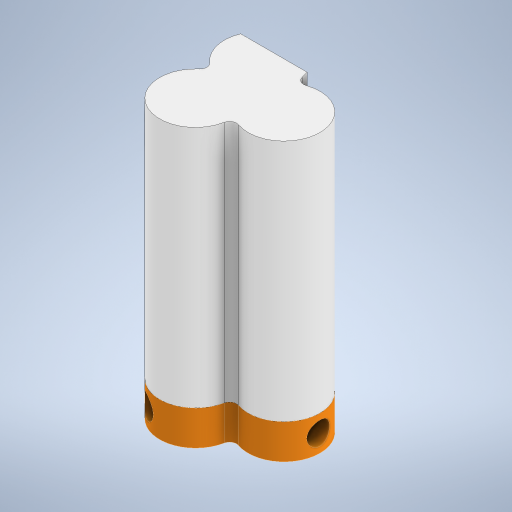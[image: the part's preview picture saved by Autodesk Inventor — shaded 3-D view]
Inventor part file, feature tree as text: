
AUTODESK INVENTOR PART (.ipt)
format: ipt  version: 2024 (Build 280153000, 153)  size: 8,383,488 bytes
history: native  units: mm
features: extrude x27, projected_geometry x22, sketch x18, other x14, plane x8, boolean_combine x8, helix x2, pattern_circular x2, fillet x1, split x1, mirror x1, imported_body x1
ambient origin geometry x8: Origin, YZ Plane, XZ Plane, XY Plane, X Axis, Y Axis, Z Axis, Center Point
bodies: Solid27 (feature_tree)
feature tree (105):
  other  "Soft Robot - Cuerpo"
  extrude  "Extrusion47"  TaperAngle=120.0deg  [1 undecoded]
  fillet  "Fillet7"  Radius=25.0mm
  other  "Work Axis3"
  plane  "Work Plane11"
  plane  "Work Plane12"
  sketch  "Sketch32"  dims[d205=3.0mm]
  helix  "Coil4"  [1 undecoded]
  helix  "Coil5"  [1 undecoded]
  plane  "Work Plane13"
  pattern_circular  "Circular Pattern5"  Count=10  [1 undecoded]
  extrude  "Extrusion51"  Depth=10.0mm TaperAngle=0.0deg
  extrude  "Extrusion55"  [1 undecoded]
  boolean_combine  "Combine16"
  extrude  "Extrusion56"  Depth=10.0mm TaperAngle=0.0deg
  boolean_combine  "Combine17"
  plane  "Work Plane17"
  plane  "Work Plane18"
  plane  "Work Plane19"
  split  "Split3"
  extrude  "Extrusion57"  Depth=5.0mm TaperAngle=0.0deg
  boolean_combine  "Combine18"
  extrude  "Extrusion58"  TaperAngle=0.0deg  [1 undecoded]
  boolean_combine  "Combine19"
  sketch  "Sketch44"  dims[d277=5.5mm]
  extrude  "Extrusion59"  Depth=1.0mm
  extrude  "Extrusion60"  Depth=0.1mm
  extrude  "Extrusion61"  Depth=0.5mm TaperAngle=0.0deg
  sketch  "Sketch45"  dims[d278=2.5mm]
  extrude  "Extrusion62"  Depth=0.5mm TaperAngle=0.0deg
  extrude  "Extrusion63"  Depth=10.0mm TaperAngle=0.0deg
  sketch  "Sketch46"  dims[d285=3.0mm d286=100.0mm d287=0.0mm]
  extrude  "Extrusion64"  Depth=0.5mm TaperAngle=0.0deg
  extrude  "Extrusion65"  Depth=0.5mm TaperAngle=0.0deg
  sketch  "Sketch47"  dims[d288=30.0mm d289=360.0deg d291=10.0mm d292=0.0mm]
  extrude  "Extrusion66"  Depth=0.5mm
  plane  "Work Plane20"
  extrude  "Extrusion68"  Depth=0.5mm
  mirror  "Mirror6"
  extrude  "Extrusion69"  Depth=0.5mm TaperAngle=0.0deg
  extrude  "Extrusion70"  Depth=10.0mm
  sketch  "Sketch50"  dims[d295=200.0mm d296=10.0mm d297=0.0mm]
  extrude  "Extrusion71"  TaperAngle=0.0deg  [1 undecoded]
  extrude  "Extrusion72"  Depth=10.0mm TaperAngle=0.0deg
  extrude  "Extrusion73"  Depth=0.5mm
  plane  "Work Plane21"
  extrude  "Extrusion74"  Depth=0.5mm
  pattern_circular  "Circular Pattern6"  [2 undecoded]
  sketch  "Sketch52"  dims[d304=10.0mm d305=0.0mm d306=0.0mm d307=0.0mm]
  extrude  "Extrusion77"  Depth=10.0mm TaperAngle=0.0deg
  extrude  "Extrusion78"  Depth=0.5mm TaperAngle=0.0deg
  extrude  "Extrusion79"  Depth=10.0mm TaperAngle=0.0deg
  boolean_combine  "Combine22"
  boolean_combine  "Combine23"
  boolean_combine  "Combine24"
  boolean_combine  "Combine25"
  extrude  "Extrusion80"  Depth=2.6mm
  extrude  "Extrusion81"  Depth=0.5mm
  extrude  "Extrusion82"  Depth=10.0mm TaperAngle=0.0deg
  sketch  "Sketch5"  dims[d47=120.0deg d48=120.0deg d49=25.0mm d50=3.0mm d203=100.0mm d204=0.0mm]
  sketch  "Sketch36"  dims[d235=0.0mm]
  projected_geometry  "Projected Loop43"
  projected_geometry  "Projected Loop46"
  sketch  "Sketch40"  dims[d238=12.0mm d239=89.0mm d240=80.0mm d241=0.0mm d242=90.0deg d243=90.0deg d244=90.0deg d245=90.0deg d246=12.0mm d247=89.0mm d248=80.0mm d249=0.0mm d250=90.0deg d251=90.0deg d252=90.0deg d253=90.0deg d254=90.0deg]
  projected_geometry  "Projected Loop47"
  other  "Moldes - Insertos PVA"
  sketch  "Sketch41"  dims[d258=3.0mm]
  projected_geometry  "Projected Loop48"
  sketch  "Sketch42"  dims[d271=1.5mm]
  sketch  "Sketch43"  dims[d273=218.25mm d274=0.0mm]
  projected_geometry  "Projected Loop49"
  other  "Soft Robot - Tapas"
  projected_geometry  "Projected Loop50"
  projected_geometry  "Projected Loop51"
  projected_geometry  "Projected Loop52"
  projected_geometry  "Projected Loop53"
  other  "Moldes - Tapa Inferior"
  projected_geometry  "Projected Loop54"
  projected_geometry  "Projected Loop55"
  projected_geometry  "Projected Loop56"
  projected_geometry  "Projected Loop57"
  projected_geometry  "Projected Loop58"
  projected_geometry  "Projected Loop59"
  projected_geometry  "Projected Loop60"
  sketch  "Sketch49"  dims[d293=-5.5mm d294=-5.5mm]
  other  "Moldes - Vaso"
  projected_geometry  "Projected Loop62"
  projected_geometry  "Projected Loop63"
  projected_geometry  "Projected Loop64"
  projected_geometry  "Projected Loop65"
  imported_body  "Base"
  sketch  "Sketch51"  dims[d298=10.0mm d299=0.0mm d301=5.0mm d302=0.0mm]
  other  "Simulación - Cavidad 1"
  other  "Simulación - Cavidad 2"
  other  "Simulación - Cavidad 3"
  sketch  "Sketch53"  dims[d308=12.0mm d309=1.0mm]
  projected_geometry  "Projected Loop66"
  other  "Simulación - Parte Exterior"
  sketch  "Sketch54"  dims[d310=0.1mm d311=0.1mm]
  projected_geometry  "Projected Loop67"
  other  "Simulación - FR"
  sketch  "Sketch55"  dims[d312=0.1mm d313=15.0mm d314=0.0mm d315=14.5mm d316=0.0mm d317=10.0mm d318=0.0mm d319=9.5mm d320=0.0mm d322=1.0mm d323=0.0mm d326=0.4mm d327=1.0mm d328=1.0mm d329=0.0mm d330=10.0mm d331=0.0mm d332=0.0mm d333=10.0mm d334=0.0mm d335=1.0mm d336=1.0mm d337=1.0mm d338=10.0mm d339=0.0mm d340=15.0mm d341=0.0mm d342=10.0mm d343=0.0mm d344=2.6mm d345=9.8mm d346=10.0mm d347=0.0mm d348=30.0mm d349=360.0deg d355=150.0mm d356=0.0mm d357=150.0mm d358=0.0mm d359=150.0mm d360=0.0mm d361=150.0mm d362=0.0mm d363=5.0mm d364=5.0mm d365=0.0mm d366=5.0mm d367=5.0mm d368=0.0mm d22=0.0mm d23=0.0mm d24=0.0mm d25=0.0mm d132=0.5mm d133=0.872665mm d134=0.5mm d135=0.872665mm d300=0.5mm]
  other  "Simulación - ROI"
  other  "Moldes - Tapa Superior"
  other  "Adaptadores"
note: 9 required parameter values undecoded (feature->parameter linkage not recoverable at this tier; creation-order binding heuristic only, values carry confidence <= 0.55)
